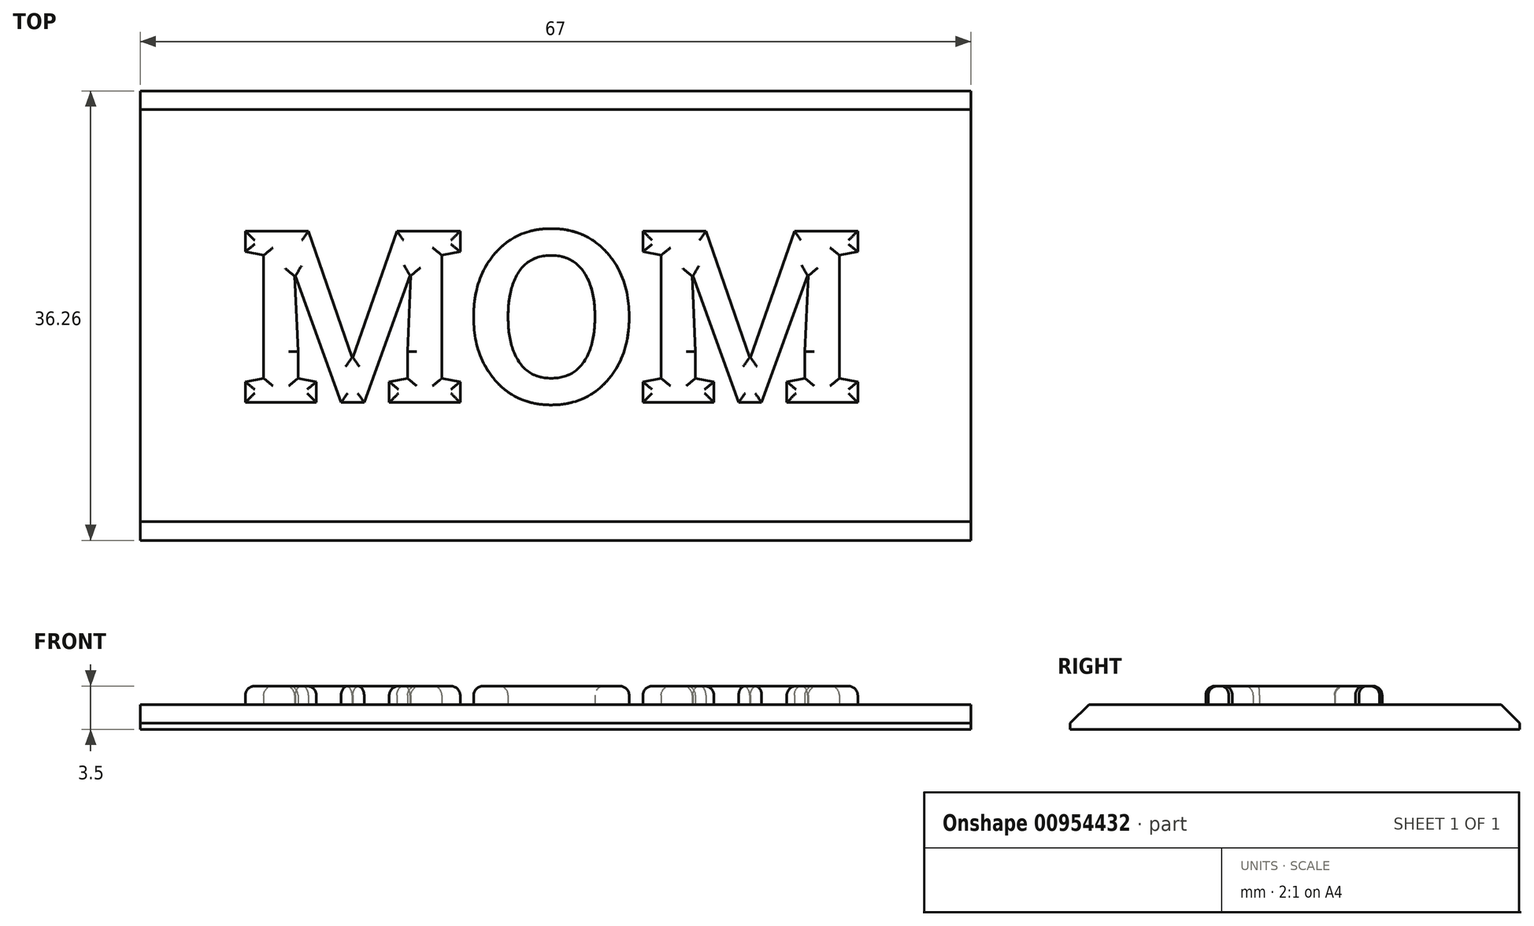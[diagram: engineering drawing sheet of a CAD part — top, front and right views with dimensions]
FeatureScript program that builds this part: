
annotation { "Feature Type Name" : "Feature", "Feature Type Description" : "" }
export const myFeature = defineFeature(function(context is Context, id is Id, definition is map)
    precondition{}
    {
        {
            var Q0;
            Q0=qCreatedBy(makeId("Top.planeOp"),FACE);
            var sketch = newSketch(context, id + "F0", { "sketchPlane" : qUnion([Q0])});
            skLineSegment(sketch, "E0.bottom", {"start": v(33.5, -18.12) * mm, "end": v(-33.5, -18.13) * mm});
            skLineSegment(sketch, "E0.top", {"start": v(33.5, 18.13) * mm, "end": v(-33.5, 18.12) * mm});
            skLineSegment(sketch, "E0.left", {"start": v(33.5, -18.12) * mm, "end": v(33.5, 18.13) * mm});
            skLineSegment(sketch, "E0.right", {"start": v(-33.5, -18.13) * mm, "end": v(-33.5, 18.12) * mm});
            skPoint(sketch, "E0.middle", {"position": v(0, 0) * mm});
            skSolve(sketch);
        }
        {
            var Q0;
            Q0 = qSketchRegion(id + "F0", true);
            extrude(context, id + "F1", {"entities" : qUnion([Q0]), "depth" : 2 * mm, "offsetDistance" : 25 * mm});
        }
        {
            var Q0;
            Q0=makeQuery(id+"F1.opExtrude","CAP_FACE",FACE,{"disambiguationData":[OSD([sQuery(id+"F0.wireOp",EDGE,"E0.bottom"),sQuery(id+"F0.wireOp",EDGE,"E0.top"),sQuery(id+"F0.wireOp",EDGE,"E0.left"),sQuery(id+"F0.wireOp",EDGE,"E0.right")])],"isStart":false});
            var sketch = newSketch(context, id + "F2", { "sketchPlane" : qUnion([Q0])});
            skText(sketch, "E1", { "text": "MOM", "fontName": "RobotoSlab-Bold.ttf"});
            skLineSegment(sketch, "E2", {"start": v(-25.56, 7) * mm, "end": v(-33.5, 18.12) * mm, "construction": true});
            skLineSegment(sketch, "E3", {"start": v(-25.56, -7) * mm, "end": v(-33.5, -18.12) * mm, "construction": true});
            skLineSegment(sketch, "E4", {"start": v(25.56, -7) * mm, "end": v(33.5, -18.13) * mm, "construction": true});
            skLineSegment(sketch, "E5", {"start": v(25.56, 7) * mm, "end": v(33.5, 18.13) * mm, "construction": true});
            const initialGuessF2  = {"E1": [-0.02556, -0.007, 1, 0, 0.014]};
            skSetInitialGuess(sketch, initialGuessF2);
            skSolve(sketch);
        }
        {
            var Q0;
            Q0 = qSketchRegion(id + "F2", true);
            extrude(context, id + "F3", {"entities" : qUnion([Q0]), "operationType" : NewBodyOperationType.ADD, "depth" : 1.5 * mm, "offsetDistance" : 25 * mm});
        }
        {
            var Q0;
            Q0=makeQuery(id+"F1.opExtrude","CAP_EDGE",EDGE,{"disambiguationData":[OSD([sQuery(id+"F0.wireOp",EDGE,"E0.bottom")])],"isStart":false});
            var Q1;
            Q1=makeQuery(id+"F1.opExtrude","CAP_EDGE",EDGE,{"disambiguationData":[OSD([sQuery(id+"F0.wireOp",EDGE,"E0.top")])],"isStart":false});
            chamfer(context, id + "F4", {"entities" : qUnion([Q0, Q1]), "width" : 1.5 * mm, "tangentPropagation" : true});
        }
        {
            var Q0;
            Q0=makeQuery(id+"F3.opExtrude","CAP_FACE",FACE,{"disambiguationData":[OSD([sQuery(id+"F2.wireOp",EDGE,"E1.sketch_text.stroke-0"),sQuery(id+"F2.wireOp",EDGE,"E1.sketch_text.stroke-1"),sQuery(id+"F2.wireOp",EDGE,"E1.sketch_text.stroke-2"),sQuery(id+"F2.wireOp",EDGE,"E1.sketch_text.stroke-3"),sQuery(id+"F2.wireOp",EDGE,"E1.sketch_text.stroke-4"),sQuery(id+"F2.wireOp",EDGE,"E1.sketch_text.stroke-5"),sQuery(id+"F2.wireOp",EDGE,"E1.sketch_text.stroke-6"),sQuery(id+"F2.wireOp",EDGE,"E1.sketch_text.stroke-7"),sQuery(id+"F2.wireOp",EDGE,"E1.sketch_text.stroke-8"),sQuery(id+"F2.wireOp",EDGE,"E1.sketch_text.stroke-9"),sQuery(id+"F2.wireOp",EDGE,"E1.sketch_text.stroke-10"),sQuery(id+"F2.wireOp",EDGE,"E1.sketch_text.stroke-11"),sQuery(id+"F2.wireOp",EDGE,"E1.sketch_text.stroke-12"),sQuery(id+"F2.wireOp",EDGE,"E1.sketch_text.stroke-13"),sQuery(id+"F2.wireOp",EDGE,"E1.sketch_text.stroke-14"),sQuery(id+"F2.wireOp",EDGE,"E1.sketch_text.stroke-15"),sQuery(id+"F2.wireOp",EDGE,"E1.sketch_text.stroke-16"),sQuery(id+"F2.wireOp",EDGE,"E1.sketch_text.stroke-17"),sQuery(id+"F2.wireOp",EDGE,"E1.sketch_text.stroke-18"),sQuery(id+"F2.wireOp",EDGE,"E1.sketch_text.stroke-19"),sQuery(id+"F2.wireOp",EDGE,"E1.sketch_text.stroke-20"),sQuery(id+"F2.wireOp",EDGE,"E1.sketch_text.stroke-21"),sQuery(id+"F2.wireOp",EDGE,"E1.sketch_text.stroke-22"),sQuery(id+"F2.wireOp",EDGE,"E1.sketch_text.stroke-23"),sQuery(id+"F2.wireOp",EDGE,"E1.sketch_text.stroke-24"),sQuery(id+"F2.wireOp",EDGE,"E1.sketch_text.stroke-25"),sQuery(id+"F2.wireOp",EDGE,"E1.sketch_text.stroke-26"),sQuery(id+"F2.wireOp",EDGE,"E1.sketch_text.stroke-27"),sQuery(id+"F2.wireOp",EDGE,"E1.sketch_text.stroke-28"),sQuery(id+"F2.wireOp",EDGE,"E1.sketch_text.stroke-29"),sQuery(id+"F2.wireOp",EDGE,"E1.sketch_text.stroke-30")])],"isStart":false});
            var Q1;
            Q1=makeQuery(id+"F3.opExtrude","CAP_FACE",FACE,{"disambiguationData":[OSD([sQuery(id+"F2.wireOp",EDGE,"E1.sketch_text.stroke-31"),sQuery(id+"F2.wireOp",EDGE,"E1.sketch_text.stroke-32"),sQuery(id+"F2.wireOp",EDGE,"E1.sketch_text.stroke-33"),sQuery(id+"F2.wireOp",EDGE,"E1.sketch_text.stroke-34"),sQuery(id+"F2.wireOp",EDGE,"E1.sketch_text.stroke-35"),sQuery(id+"F2.wireOp",EDGE,"E1.sketch_text.stroke-36"),sQuery(id+"F2.wireOp",EDGE,"E1.sketch_text.stroke-37"),sQuery(id+"F2.wireOp",EDGE,"E1.sketch_text.stroke-38"),sQuery(id+"F2.wireOp",EDGE,"E1.sketch_text.stroke-39"),sQuery(id+"F2.wireOp",EDGE,"E1.sketch_text.stroke-40"),sQuery(id+"F2.wireOp",EDGE,"E1.sketch_text.stroke-41"),sQuery(id+"F2.wireOp",EDGE,"E1.sketch_text.stroke-42"),sQuery(id+"F2.wireOp",EDGE,"E1.sketch_text.stroke-43"),sQuery(id+"F2.wireOp",EDGE,"E1.sketch_text.stroke-44"),sQuery(id+"F2.wireOp",EDGE,"E1.sketch_text.stroke-45"),sQuery(id+"F2.wireOp",EDGE,"E1.sketch_text.stroke-46"),sQuery(id+"F2.wireOp",EDGE,"E1.sketch_text.stroke-47"),sQuery(id+"F2.wireOp",EDGE,"E1.sketch_text.stroke-48"),sQuery(id+"F2.wireOp",EDGE,"E1.sketch_text.stroke-49"),sQuery(id+"F2.wireOp",EDGE,"E1.sketch_text.stroke-50")])],"isStart":false});
            var Q2;
            Q2=makeQuery(id+"F3.opExtrude","CAP_FACE",FACE,{"disambiguationData":[OSD([sQuery(id+"F2.wireOp",EDGE,"E1.sketch_text.stroke-51"),sQuery(id+"F2.wireOp",EDGE,"E1.sketch_text.stroke-52"),sQuery(id+"F2.wireOp",EDGE,"E1.sketch_text.stroke-53"),sQuery(id+"F2.wireOp",EDGE,"E1.sketch_text.stroke-54"),sQuery(id+"F2.wireOp",EDGE,"E1.sketch_text.stroke-55"),sQuery(id+"F2.wireOp",EDGE,"E1.sketch_text.stroke-56"),sQuery(id+"F2.wireOp",EDGE,"E1.sketch_text.stroke-57"),sQuery(id+"F2.wireOp",EDGE,"E1.sketch_text.stroke-58"),sQuery(id+"F2.wireOp",EDGE,"E1.sketch_text.stroke-59"),sQuery(id+"F2.wireOp",EDGE,"E1.sketch_text.stroke-60"),sQuery(id+"F2.wireOp",EDGE,"E1.sketch_text.stroke-61"),sQuery(id+"F2.wireOp",EDGE,"E1.sketch_text.stroke-62"),sQuery(id+"F2.wireOp",EDGE,"E1.sketch_text.stroke-63"),sQuery(id+"F2.wireOp",EDGE,"E1.sketch_text.stroke-64"),sQuery(id+"F2.wireOp",EDGE,"E1.sketch_text.stroke-65"),sQuery(id+"F2.wireOp",EDGE,"E1.sketch_text.stroke-66"),sQuery(id+"F2.wireOp",EDGE,"E1.sketch_text.stroke-67"),sQuery(id+"F2.wireOp",EDGE,"E1.sketch_text.stroke-68"),sQuery(id+"F2.wireOp",EDGE,"E1.sketch_text.stroke-69"),sQuery(id+"F2.wireOp",EDGE,"E1.sketch_text.stroke-70"),sQuery(id+"F2.wireOp",EDGE,"E1.sketch_text.stroke-71"),sQuery(id+"F2.wireOp",EDGE,"E1.sketch_text.stroke-72"),sQuery(id+"F2.wireOp",EDGE,"E1.sketch_text.stroke-73"),sQuery(id+"F2.wireOp",EDGE,"E1.sketch_text.stroke-74"),sQuery(id+"F2.wireOp",EDGE,"E1.sketch_text.stroke-75"),sQuery(id+"F2.wireOp",EDGE,"E1.sketch_text.stroke-76"),sQuery(id+"F2.wireOp",EDGE,"E1.sketch_text.stroke-77"),sQuery(id+"F2.wireOp",EDGE,"E1.sketch_text.stroke-78"),sQuery(id+"F2.wireOp",EDGE,"E1.sketch_text.stroke-79"),sQuery(id+"F2.wireOp",EDGE,"E1.sketch_text.stroke-80"),sQuery(id+"F2.wireOp",EDGE,"E1.sketch_text.stroke-81")])],"isStart":false});
            fillet(context, id + "F5", {"entities" : qUnion([Q0, Q1, Q2]), "radius" : .75 * mm, "tangentPropagation" : true, "allowEdgeOverflow" : false});
        }
    });
